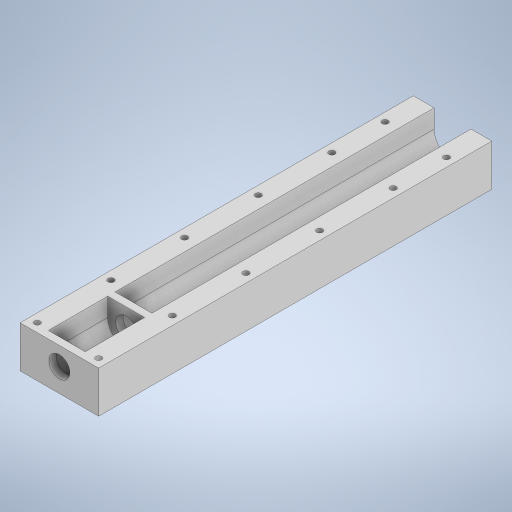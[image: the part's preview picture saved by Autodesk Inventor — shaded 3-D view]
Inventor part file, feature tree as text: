
AUTODESK INVENTOR PART (.ipt)
format: ipt  version: 2023 (Build 270158000, 158)  size: 313,856 bytes
history: native  units: mm
features: sketch x6, extrude x4, hole x2, projected_geometry x1
ambient origin geometry x8: Origin, YZ Plane, XZ Plane, XY Plane, X Axis, Y Axis, Z Axis, Center Point
bodies: Solid1 (feature_tree)
feature tree (13):
  extrude  "Extrusion1"  Depth=24.2mm TaperAngle=0.0deg
  extrude  "Extrusion3"  Depth=32.0mm
  extrude  "Extrusion4"  Depth=3.0mm TaperAngle=0.0deg
  extrude  "Extrusion5"  Depth=130.0mm TaperAngle=0.0deg
  hole  "Hole1"  [1 undecoded]
  hole  "Hole3"  [1 undecoded]
  sketch  "Sketch1"  dims[d0=15.0mm d3=24.2mm d4=0.0mm]
  sketch  "Sketch2"  dims[d5=32.0mm d6=2.0mm]
  projected_geometry  "Projected Loop1"
  sketch  "Sketch4"  dims[d10=8.5mm d11=3.0mm d12=0.0mm]
  sketch  "Sketch5"  dims[d13=3.0mm d14=0.0mm d15=130.0mm d16=0.0mm]
  sketch  "Sketch6"  dims[d17=3.5mm d18=3.5mm]
  sketch  "Sketch7"  dims[d19=2.38125mm d20=6.0mm d21=4.0mm d22=2.0mm d23=90.0deg d24=10.0mm d25=20.594885mm d27=3.5mm d42=50.0mm d44=30.0mm d45=10.0mm d47=10.0mm d49=3.5mm d50=15.0mm d51=2.38125mm d52=6.0mm d53=4.0mm d54=2.0mm d55=90.0deg d56=10.0mm d57=20.594885mm]
note: 2 required parameter values undecoded (feature->parameter linkage not recoverable at this tier; creation-order binding heuristic only, values carry confidence <= 0.55)
